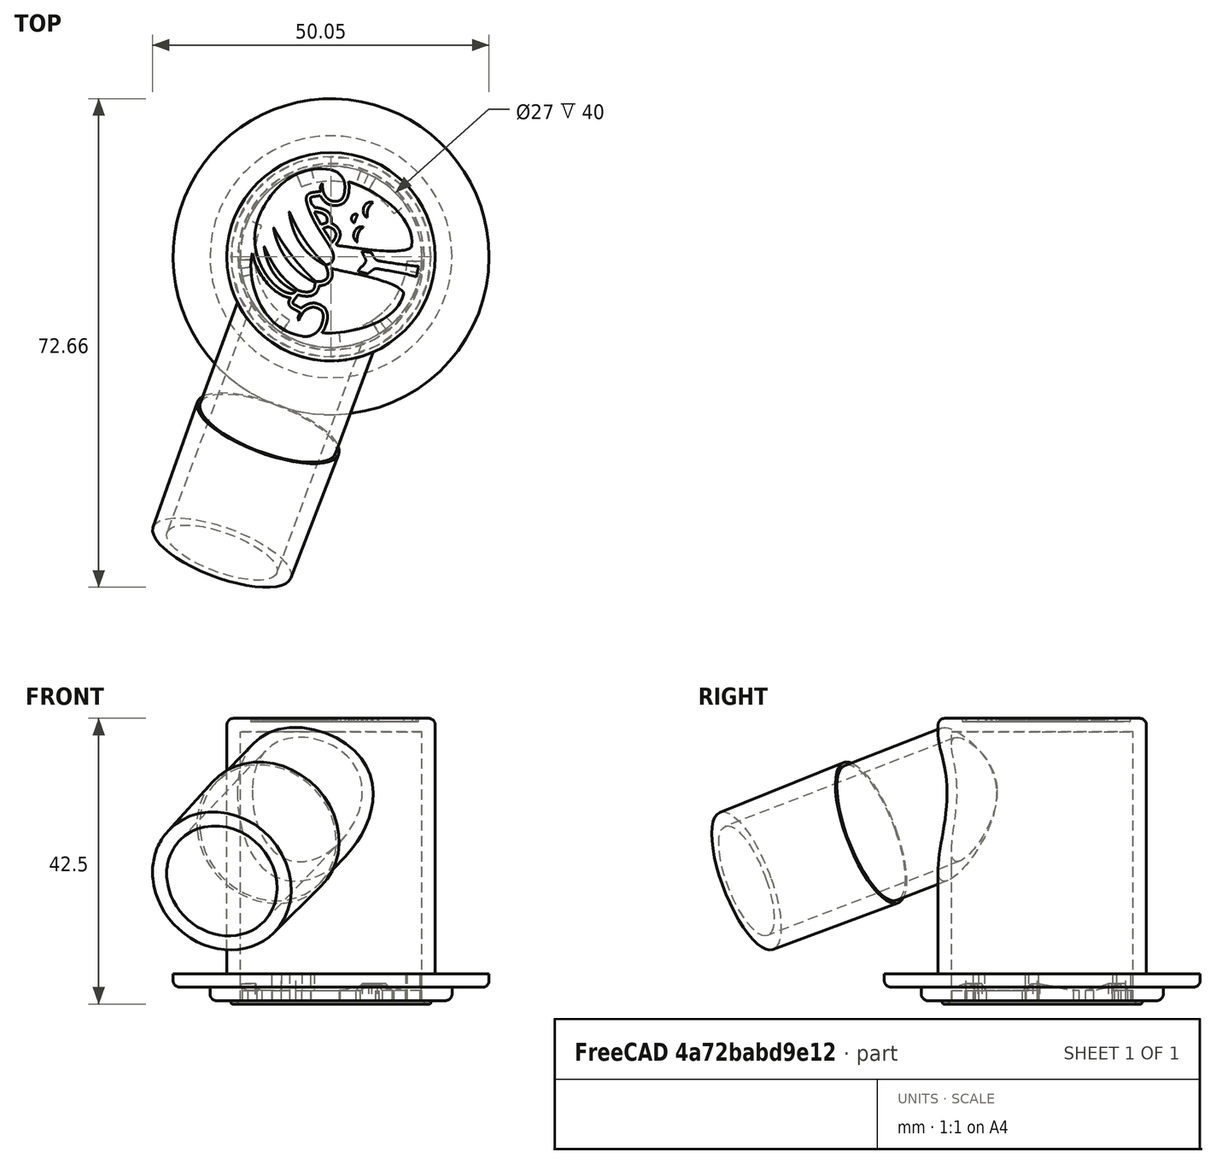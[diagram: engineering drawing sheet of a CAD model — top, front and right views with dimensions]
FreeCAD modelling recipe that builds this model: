
FCSTD DOCUMENT  (FreeCAD 0.18R4 (GitTag))
Label: PAPR-MaskAdapter-V2
License: All rights reserved
LicenseURL: http://en.wikipedia.org/wiki/All_rights_reserved
objects: Sketcher::SketchObject×40, Part::Sweep×16, Part::MultiFuse×13, Part::Feature×10, Part::Extrusion×10, Part::Cylinder×6, Part::Mirroring×5, Part::Fillet×4, Part::Cut×4, Part::FeaturePython×2, PartDesign::Body×1, Mesh::Feature×1, Part::Cone×1
note: 112 computed .brp shape members not serialized (recipe doc carries the construction recipe); baked Part::Feature solids carry a one-line shape summary decoded from their .brp

FEATURE [Sketcher::SketchObject] Sketch  label="RampStart"
  Placement = pos=(0,0,0) rot=(1,0,0;1.5708rad)
  sketch-geometry (4):
    g0: LineSegment StartX=-13.5 StartY=0 StartZ=0 EndX=-13.5 EndY=1.5 EndZ=0
    g1: LineSegment StartX=-13.5 StartY=1.5 StartZ=0 EndX=-11.3 EndY=1.5 EndZ=0
    g2: LineSegment StartX=-11.3 StartY=1.5 StartZ=0 EndX=-11.3 EndY=0 EndZ=0
    g3: LineSegment StartX=-11.3 StartY=0 StartZ=0 EndX=-13.5 EndY=0 EndZ=0
  constraints (12):
    c: Coincident(g0,g1)
    c: Coincident(g1,g2)
    c: Coincident(g2,g3)
    c: Coincident(g3,g0)
    c: Parallel(g0,g2)
    c: Parallel(g1,g3)
    c: Horizontal(g3)
    c: Vertical(g2)
    c: DistanceY(g-1,g2) = 0
    c: DistanceX(g2,g-1) = 11.3
    c: DistanceX(g0,g-1) = 13.5
    c: DistanceY(g0,g0) = 1.5
FEATURE [Sketcher::SketchObject] Sketch001  label="InnerCircumference"
  Placement = pos=(0,0,0) rot=(1,0,0;3.14159rad)
  sketch-geometry (1):
    g0: Circle CenterX=0 CenterY=0 CenterZ=0 NormalX=0 NormalY=0 NormalZ=1 AngleXU=0 Radius=11
  constraints (1):
    c: Radius(g0) = 11
FEATURE [Sketcher::SketchObject] Sketch002  label="RampEnd"
  Placement = pos=(0,0,0) rot=(0.950615,-0.219467,-0.219467;1.62142rad)
  sketch-geometry (4):
    g0: LineSegment StartX=-13.5 StartY=0 StartZ=0 EndX=-13.5 EndY=2.5 EndZ=0
    g1: LineSegment StartX=-13.5 StartY=2.5 StartZ=0 EndX=-11.3 EndY=2.5 EndZ=0
    g2: LineSegment StartX=-11.3 StartY=2.5 StartZ=0 EndX=-11.3 EndY=0 EndZ=0
    g3: LineSegment StartX=-11.3 StartY=0 StartZ=0 EndX=-13.5 EndY=0 EndZ=0
  constraints (12):
    c: Coincident(g0,g1)
    c: Coincident(g1,g2)
    c: Coincident(g2,g3)
    c: Coincident(g3,g0)
    c: Parallel(g0,g2)
    c: Parallel(g1,g3)
    c: Horizontal(g3)
    c: Vertical(g2)
    c: DistanceY(g-1,g2) = 0
    c: DistanceX(g2,g-1) = 11.3
    c: DistanceX(g0,g-1) = 13.5
    c: DistanceY(g0,g0) = 2.5
FEATURE [Sketcher::SketchObject] Sketch003  label="RampFlat"
  Placement = pos=(0,0,0) rot=(0.930118,-0.259693,-0.259693;1.64318rad)
  sketch-geometry (4):
    g0: LineSegment StartX=-13.5 StartY=0 StartZ=0 EndX=-13.5 EndY=2.5 EndZ=0
    g1: LineSegment StartX=-13.5 StartY=2.5 StartZ=0 EndX=-11.3 EndY=2.5 EndZ=0
    g2: LineSegment StartX=-11.3 StartY=2.5 StartZ=0 EndX=-11.3 EndY=0 EndZ=0
    g3: LineSegment StartX=-11.3 StartY=0 StartZ=0 EndX=-13.5 EndY=0 EndZ=0
  constraints (12):
    c: Coincident(g0,g1)
    c: Coincident(g1,g2)
    c: Coincident(g2,g3)
    c: Coincident(g3,g0)
    c: Parallel(g0,g2)
    c: Parallel(g1,g3)
    c: Horizontal(g3)
    c: Vertical(g2)
    c: DistanceY(g-1,g2) = 0
    c: DistanceX(g2,g-1) = 11.3
    c: DistanceX(g0,g-1) = 13.5
    c: DistanceY(g0,g0) = 2.5
FEATURE [Sketcher::SketchObject] Sketch004  label="LockFlat"
  Placement = pos=(0,0,0) rot=(0.906297,-0.298852,-0.298852;1.66903rad)
  sketch-geometry (4):
    g0: LineSegment StartX=-13.5 StartY=0 StartZ=0 EndX=-13.5 EndY=1.5 EndZ=0
    g1: LineSegment StartX=-13.5 StartY=1.5 StartZ=0 EndX=-11.3 EndY=1.5 EndZ=0
    g2: LineSegment StartX=-11.3 StartY=1.5 StartZ=0 EndX=-11.3 EndY=0 EndZ=0
    g3: LineSegment StartX=-11.3 StartY=0 StartZ=0 EndX=-13.5 EndY=0 EndZ=0
  constraints (12):
    c: Coincident(g0,g1)
    c: Coincident(g1,g2)
    c: Coincident(g2,g3)
    c: Coincident(g3,g0)
    c: Parallel(g0,g2)
    c: Parallel(g1,g3)
    c: Horizontal(g3)
    c: Vertical(g2)
    c: DistanceY(g-1,g2) = 0
    c: DistanceX(g2,g-1) = 11.3
    c: DistanceX(g0,g-1) = 13.5
    c: DistanceY(g0,g0) = 1.5
FEATURE [Sketcher::SketchObject] Sketch005  label="LockFlatEnd"
  Placement = pos=(0,0,0) rot=(0.638387,-0.544271,-0.544271;2.00526rad)
  sketch-geometry (4):
    g0: LineSegment StartX=-13.5 StartY=0 StartZ=0 EndX=-13.5 EndY=1.5 EndZ=0
    g1: LineSegment StartX=-13.5 StartY=1.5 StartZ=0 EndX=-11.3 EndY=1.5 EndZ=0
    g2: LineSegment StartX=-11.3 StartY=1.5 StartZ=0 EndX=-11.3 EndY=0 EndZ=0
    g3: LineSegment StartX=-11.3 StartY=0 StartZ=0 EndX=-13.5 EndY=0 EndZ=0
  constraints (12):
    c: Coincident(g0,g1)
    c: Coincident(g1,g2)
    c: Coincident(g2,g3)
    c: Coincident(g3,g0)
    c: Parallel(g0,g2)
    c: Parallel(g1,g3)
    c: Horizontal(g3)
    c: Vertical(g2)
    c: DistanceY(g-1,g2) = 0
    c: DistanceX(g2,g-1) = 11.3
    c: DistanceX(g0,g-1) = 13.5
    c: DistanceY(g0,g0) = 1.5
FEATURE [Sketcher::SketchObject] Sketch006  label="RampPath"
  sketch-geometry (1):
    g0: ArcOfCircle CenterX=0 CenterY=0 CenterZ=0 NormalX=0 NormalY=0 NormalZ=1 AngleXU=0 Radius=11.0109 StartAngle=1.68589 EndAngle=3.14182
FEATURE [Sketcher::SketchObject] Sketch007  label="Path1"
  sketch-geometry (2):
    g0: ArcOfCircle CenterX=0 CenterY=0 CenterZ=0 NormalX=0 NormalY=0 NormalZ=1 AngleXU=0 Radius=11.3 StartAngle=2.68754 EndAngle=3.14132
    g1: GeomPoint X=-10.1564 Y=4.95359 Z=0
  constraints (3):
    c: Radius(g0) = 11.3
    c: Coincident(g-1,g0)
    c: Angle(g0) = 0.453786
FEATURE [PartDesign::Body] Body
  Group = -> [Sketch005,Sketch004,Sketch003,Sketch002,Sketch001,Sketch,Sketch006,Sketch007]
  Origin = -> Origin
FEATURE [Part::Sweep] Sweep
  Frenet = false
  Sections = -> [Sketch,Sketch002]
  Solid = true
  Spine = -> Sketch007 [Edge1]
  Transition = 1
FEATURE [Sketcher::SketchObject] Sketch008  label="Path2"
  sketch-geometry (1):
    g0: ArcOfCircle CenterX=0 CenterY=0 CenterZ=0 NormalX=0 NormalY=0 NormalZ=1 AngleXU=0 Radius=11.3 StartAngle=2.59707 EndAngle=2.68754
  constraints (2):
    c: Radius(g0) = 11.3
    c: Coincident(g0,g-1)
FEATURE [Sketcher::SketchObject] Sketch009  label="Path3"
  sketch-geometry (1):
    g0: ArcOfCircle CenterX=0 CenterY=0 CenterZ=0 NormalX=0 NormalY=0 NormalZ=1 AngleXU=0 Radius=11.3 StartAngle=2.50468 EndAngle=2.59704
  constraints (2):
    c: Radius(g0) = 11.3
    c: Coincident(g0,g-1)
FEATURE [Sketcher::SketchObject] Sketch010  label="Path4"
  sketch-geometry (1):
    g0: ArcOfCircle CenterX=0 CenterY=0 CenterZ=0 NormalX=0 NormalY=0 NormalZ=1 AngleXU=0 Radius=11.3 StartAngle=1.72935 EndAngle=2.50452
  constraints (2):
    c: Radius(g0) = 11.3
    c: Coincident(g0,g-1)
FEATURE [Part::Sweep] Sweep001
  Frenet = false
  Sections = -> [Sketch002,Sketch003]
  Solid = true
  Spine = -> Sketch008 [Edge1]
  Transition = 1
FEATURE [Part::Sweep] Sweep002
  Frenet = false
  Sections = -> [Sketch003,Sketch004]
  Solid = true
  Spine = -> Sketch009 [Edge1]
  Transition = 1
FEATURE [Part::Sweep] Sweep003
  Frenet = false
  Sections = -> [Sketch004,Sketch005]
  Solid = true
  Spine = -> Sketch010 [Edge1]
  Transition = 1
FEATURE [Part::MultiFuse] Fusion  label="Ramp"
  Shapes = -> [Sweep,Sweep001,Sweep002,Sweep003]
FEATURE [Sketcher::SketchObject] Sketch011  label="EndstopEnd"
  Placement = pos=(0,0,0) rot=(0.638387,-0.544271,-0.544271;2.00526rad)
  sketch-geometry (4):
    g0: LineSegment StartX=-13.5 StartY=0 StartZ=0 EndX=-13.5 EndY=4 EndZ=0
    g1: LineSegment StartX=-13.5 StartY=4 StartZ=0 EndX=-11.3 EndY=4 EndZ=0
    g2: LineSegment StartX=-11.3 StartY=4 StartZ=0 EndX=-11.3 EndY=0 EndZ=0
    g3: LineSegment StartX=-11.3 StartY=0 StartZ=0 EndX=-13.5 EndY=0 EndZ=0
  constraints (12):
    c: Coincident(g0,g1)
    c: Coincident(g1,g2)
    c: Coincident(g2,g3)
    c: Coincident(g3,g0)
    c: Parallel(g0,g2)
    c: Parallel(g1,g3)
    c: Horizontal(g3)
    c: Vertical(g2)
    c: DistanceY(g-1,g2) = 0
    c: DistanceX(g2,g-1) = 11.3
    c: DistanceX(g0,g-1) = 13.5
    c: DistanceY(g0,g0) = 4
FEATURE [Sketcher::SketchObject] Sketch012  label="EndstopStart"
  Placement = pos=(0,0,0) rot=(0.688237,-0.512996,-0.512996;1.93602rad)
  sketch-geometry (4):
    g0: LineSegment StartX=-13.5 StartY=0 StartZ=0 EndX=-13.5 EndY=4 EndZ=0
    g1: LineSegment StartX=-13.5 StartY=4 StartZ=0 EndX=-11.3 EndY=4 EndZ=0
    g2: LineSegment StartX=-11.3 StartY=4 StartZ=0 EndX=-11.3 EndY=0 EndZ=0
    g3: LineSegment StartX=-11.3 StartY=0 StartZ=0 EndX=-13.5 EndY=0 EndZ=0
  constraints (12):
    c: Coincident(g0,g1)
    c: Coincident(g1,g2)
    c: Coincident(g2,g3)
    c: Coincident(g3,g0)
    c: Parallel(g0,g2)
    c: Parallel(g1,g3)
    c: Horizontal(g3)
    c: Vertical(g2)
    c: DistanceY(g-1,g2) = 0
    c: DistanceX(g2,g-1) = 11.3
    c: DistanceX(g0,g-1) = 13.5
    c: DistanceY(g0,g0) = 4
FEATURE [Sketcher::SketchObject] Sketch013  label="EndstopPath"
  sketch-geometry (1):
    g0: ArcOfCircle CenterX=0 CenterY=0 CenterZ=0 NormalX=0 NormalY=0 NormalZ=1 AngleXU=0 Radius=11.3 StartAngle=1.72959 EndAngle=1.86043
  constraints (2):
    c: Radius(g0) = 11.3
    c: Coincident(g-1,g0)
FEATURE [Part::Sweep] Sweep004  label="EndStop"
  Frenet = false
  Sections = -> [Sketch012,Sketch011]
  Solid = true
  Spine = -> Sketch013 [Edge1]
  Transition = 1
FEATURE [Part::MultiFuse] Fusion001  label="RampWithEndstop"
  Shapes = -> [Fusion,Sweep004]
FEATURE [Part::Cylinder] Cylinder001  label="pBase-Lower"
  Angle = 360
  AttacherType = Attacher::AttachEngine3D
  Height = 2
  Radius = 18
FEATURE [Part::Cylinder] Cylinder002  label="nBody-Chamber"
  Angle = 360
  AttacherType = Attacher::AttachEngine3D
  Height = 40
  Radius = 13.5
FEATURE [Sketcher::SketchObject] Sketch015  label="GrooveProfile"
  Placement = pos=(0,0,0) rot=(1,0,0;1.5708rad)
  sketch-geometry (4):
    g0: LineSegment StartX=-14.875 StartY=-0.5 StartZ=0 EndX=-13.875 EndY=-0.5 EndZ=0
    g1: LineSegment StartX=-13.875 StartY=-0.5 StartZ=0 EndX=-13.875 EndY=0.5 EndZ=0
    g2: LineSegment StartX=-13.875 StartY=0.5 StartZ=0 EndX=-14.875 EndY=0.5 EndZ=0
    g3: LineSegment StartX=-14.875 StartY=0.5 StartZ=0 EndX=-14.875 EndY=-0.5 EndZ=0
  constraints (12):
    c: Coincident(g0,g1)
    c: Coincident(g1,g2)
    c: Coincident(g2,g3)
    c: Coincident(g3,g0)
    c: Horizontal(g0)
    c: Horizontal(g2)
    c: Vertical(g1)
    c: Vertical(g3)
    c: DistanceX(g0,g0) = 1
    c: Equal(g0,g1)
    c: DistanceY(g1,g-1) = -0.5
    c: DistanceX(g1,g-1) = 13.875
FEATURE [Sketcher::SketchObject] Sketch016  label="GroovePath"
  sketch-geometry (1):
    g0: Circle CenterX=0 CenterY=0 CenterZ=0 NormalX=0 NormalY=0 NormalZ=1 AngleXU=0 Radius=13.875
  constraints (2):
    c: Coincident(g0,g-1)
    c: Radius(g0) = 13.875
FEATURE [Part::Sweep] Sweep005  label="pBase-Groove"
  Frenet = false
  Sections = -> [Sketch015]
  Solid = true
  Spine = -> Sketch016 [Edge1]
  Transition = 1
FEATURE [Part::Mirroring] Part__Mirroring  label="RampWithEndstopLong1"
  Base = (2.14696,3.57628e-07,2)
  Normal = (0,1,-1.19209e-07)
  Placement = pos=(0,0,0) rot=(0,0,-1;0.418879rad)
  Source = -> Fusion001
FEATURE [Sketcher::SketchObject] Sketch017  label="RampStart001"
  Placement = pos=(0,0,0) rot=(1,0,0;1.5708rad)
  sketch-geometry (4):
    g0: LineSegment StartX=-13.5 StartY=0 StartZ=0 EndX=-13.5 EndY=1.5 EndZ=0
    g1: LineSegment StartX=-13.5 StartY=1.5 StartZ=0 EndX=-11.3 EndY=1.5 EndZ=0
    g2: LineSegment StartX=-11.3 StartY=1.5 StartZ=0 EndX=-11.3 EndY=0 EndZ=0
    g3: LineSegment StartX=-11.3 StartY=0 StartZ=0 EndX=-13.5 EndY=0 EndZ=0
  constraints (12):
    c: Coincident(g0,g1)
    c: Coincident(g1,g2)
    c: Coincident(g2,g3)
    c: Coincident(g3,g0)
    c: Parallel(g0,g2)
    c: Parallel(g1,g3)
    c: Horizontal(g3)
    c: Vertical(g2)
    c: DistanceY(g-1,g2) = 0
    c: DistanceX(g2,g-1) = 11.3
    c: DistanceX(g0,g-1) = 13.5
    c: DistanceY(g0,g0) = 1.5
FEATURE [Sketcher::SketchObject] Sketch018  label="RampEnd001"
  Placement = pos=(0,0,0) rot=(0.950615,-0.219467,-0.219467;1.62142rad)
  sketch-geometry (4):
    g0: LineSegment StartX=-13.5 StartY=0 StartZ=0 EndX=-13.5 EndY=2.5 EndZ=0
    g1: LineSegment StartX=-13.5 StartY=2.5 StartZ=0 EndX=-11.3 EndY=2.5 EndZ=0
    g2: LineSegment StartX=-11.3 StartY=2.5 StartZ=0 EndX=-11.3 EndY=0 EndZ=0
    g3: LineSegment StartX=-11.3 StartY=0 StartZ=0 EndX=-13.5 EndY=0 EndZ=0
  constraints (12):
    c: Coincident(g0,g1)
    c: Coincident(g1,g2)
    c: Coincident(g2,g3)
    c: Coincident(g3,g0)
    c: Parallel(g0,g2)
    c: Parallel(g1,g3)
    c: Horizontal(g3)
    c: Vertical(g2)
    c: DistanceY(g-1,g2) = 0
    c: DistanceX(g2,g-1) = 11.3
    c: DistanceX(g0,g-1) = 13.5
    c: DistanceY(g0,g0) = 2.5
FEATURE [Sketcher::SketchObject] Sketch019  label="RampFlat001"
  Placement = pos=(0,0,0) rot=(0.930118,-0.259693,-0.259693;1.64318rad)
  sketch-geometry (4):
    g0: LineSegment StartX=-13.5 StartY=0 StartZ=0 EndX=-13.5 EndY=2.5 EndZ=0
    g1: LineSegment StartX=-13.5 StartY=2.5 StartZ=0 EndX=-11.3 EndY=2.5 EndZ=0
    g2: LineSegment StartX=-11.3 StartY=2.5 StartZ=0 EndX=-11.3 EndY=0 EndZ=0
    g3: LineSegment StartX=-11.3 StartY=0 StartZ=0 EndX=-13.5 EndY=0 EndZ=0
  constraints (12):
    c: Coincident(g0,g1)
    c: Coincident(g1,g2)
    c: Coincident(g2,g3)
    c: Coincident(g3,g0)
    c: Parallel(g0,g2)
    c: Parallel(g1,g3)
    c: Horizontal(g3)
    c: Vertical(g2)
    c: DistanceY(g-1,g2) = 0
    c: DistanceX(g2,g-1) = 11.3
    c: DistanceX(g0,g-1) = 13.5
    c: DistanceY(g0,g0) = 2.5
FEATURE [Sketcher::SketchObject] Sketch020  label="LockFlat001"
  Placement = pos=(0,0,0) rot=(0.906297,-0.298852,-0.298852;1.66903rad)
  sketch-geometry (4):
    g0: LineSegment StartX=-13.5 StartY=0 StartZ=0 EndX=-13.5 EndY=1.5 EndZ=0
    g1: LineSegment StartX=-13.5 StartY=1.5 StartZ=0 EndX=-11.3 EndY=1.5 EndZ=0
    g2: LineSegment StartX=-11.3 StartY=1.5 StartZ=0 EndX=-11.3 EndY=0 EndZ=0
    g3: LineSegment StartX=-11.3 StartY=0 StartZ=0 EndX=-13.5 EndY=0 EndZ=0
  constraints (12):
    c: Coincident(g0,g1)
    c: Coincident(g1,g2)
    c: Coincident(g2,g3)
    c: Coincident(g3,g0)
    c: Parallel(g0,g2)
    c: Parallel(g1,g3)
    c: Horizontal(g3)
    c: Vertical(g2)
    c: DistanceY(g-1,g2) = 0
    c: DistanceX(g2,g-1) = 11.3
    c: DistanceX(g0,g-1) = 13.5
    c: DistanceY(g0,g0) = 1.5
FEATURE [Sketcher::SketchObject] Sketch021  label="LockFlatEnd001"
  Placement = pos=(0,0,0) rot=(0.656406,-0.533447,-0.533447;1.97986rad)
  sketch-geometry (4):
    g0: LineSegment StartX=-13.5 StartY=0 StartZ=0 EndX=-13.5 EndY=1.5 EndZ=0
    g1: LineSegment StartX=-13.5 StartY=1.5 StartZ=0 EndX=-11.3 EndY=1.5 EndZ=0
    g2: LineSegment StartX=-11.3 StartY=1.5 StartZ=0 EndX=-11.3 EndY=0 EndZ=0
    g3: LineSegment StartX=-11.3 StartY=0 StartZ=0 EndX=-13.5 EndY=0 EndZ=0
  constraints (12):
    c: Coincident(g0,g1)
    c: Coincident(g1,g2)
    c: Coincident(g2,g3)
    c: Coincident(g3,g0)
    c: Parallel(g0,g2)
    c: Parallel(g1,g3)
    c: Horizontal(g3)
    c: Vertical(g2)
    c: DistanceY(g-1,g2) = 0
    c: DistanceX(g2,g-1) = 11.3
    c: DistanceX(g0,g-1) = 13.5
    c: DistanceY(g0,g0) = 1.5
FEATURE [Sketcher::SketchObject] Sketch022  label="Path005"
  sketch-geometry (2):
    g0: ArcOfCircle CenterX=0 CenterY=0 CenterZ=0 NormalX=0 NormalY=0 NormalZ=1 AngleXU=0 Radius=11.3 StartAngle=2.68754 EndAngle=3.14132
    g1: GeomPoint X=-10.1564 Y=4.95359 Z=0
  constraints (3):
    c: Radius(g0) = 11.3
    c: Coincident(g-1,g0)
    c: Angle(g0) = 0.453786
FEATURE [Sketcher::SketchObject] Sketch023  label="Path006"
  sketch-geometry (1):
    g0: ArcOfCircle CenterX=0 CenterY=0 CenterZ=0 NormalX=0 NormalY=0 NormalZ=1 AngleXU=0 Radius=11.3 StartAngle=2.59707 EndAngle=2.68754
  constraints (2):
    c: Radius(g0) = 11.3
    c: Coincident(g0,g-1)
FEATURE [Sketcher::SketchObject] Sketch024  label="Path007"
  sketch-geometry (1):
    g0: ArcOfCircle CenterX=0 CenterY=0 CenterZ=0 NormalX=0 NormalY=0 NormalZ=1 AngleXU=0 Radius=11.3 StartAngle=2.50468 EndAngle=2.59704
  constraints (2):
    c: Radius(g0) = 11.3
    c: Coincident(g0,g-1)
FEATURE [Sketcher::SketchObject] Sketch025  label="Path008"
  sketch-geometry (1):
    g0: ArcOfCircle CenterX=0 CenterY=0 CenterZ=0 NormalX=0 NormalY=0 NormalZ=1 AngleXU=0 Radius=11.3 StartAngle=1.77654 EndAngle=2.50452
  constraints (2):
    c: Radius(g0) = 11.3
    c: Coincident(g0,g-1)
FEATURE [Part::Sweep] Sweep006
  Frenet = false
  Sections = -> [Sketch018,Sketch019]
  Solid = true
  Spine = -> Sketch023 [Edge1]
  Transition = 1
FEATURE [Part::Sweep] Sweep007
  Frenet = false
  Sections = -> [Sketch019,Sketch020]
  Solid = true
  Spine = -> Sketch024 [Edge1]
  Transition = 1
FEATURE [Part::Sweep] Sweep008
  Frenet = false
  Sections = -> [Sketch020,Sketch021]
  Solid = true
  Spine = -> Sketch025 [Edge1]
  Transition = 1
FEATURE [Sketcher::SketchObject] Sketch026  label="EndstopEnd001"
  Placement = pos=(0,0,0) rot=(0.656406,-0.533447,-0.533447;1.97986rad)
  sketch-geometry (4):
    g0: LineSegment StartX=-13.5 StartY=0 StartZ=0 EndX=-13.5 EndY=4 EndZ=0
    g1: LineSegment StartX=-13.5 StartY=4 StartZ=0 EndX=-11.3 EndY=4 EndZ=0
    g2: LineSegment StartX=-11.3 StartY=4 StartZ=0 EndX=-11.3 EndY=0 EndZ=0
    g3: LineSegment StartX=-11.3 StartY=0 StartZ=0 EndX=-13.5 EndY=0 EndZ=0
  constraints (12):
    c: Coincident(g0,g1)
    c: Coincident(g1,g2)
    c: Coincident(g2,g3)
    c: Coincident(g3,g0)
    c: Parallel(g0,g2)
    c: Parallel(g1,g3)
    c: Horizontal(g3)
    c: Vertical(g2)
    c: DistanceY(g-1,g2) = 0
    c: DistanceX(g2,g-1) = 11.3
    c: DistanceX(g0,g-1) = 13.5
    c: DistanceY(g0,g0) = 4
FEATURE [Sketcher::SketchObject] Sketch027  label="EndstopStart001"
  Placement = pos=(0,0,0) rot=(0.722291,-0.489028,-0.489028;1.89053rad)
  sketch-geometry (4):
    g0: LineSegment StartX=-13.5 StartY=0 StartZ=0 EndX=-13.5 EndY=4 EndZ=0
    g1: LineSegment StartX=-13.5 StartY=4 StartZ=0 EndX=-11.3 EndY=4 EndZ=0
    g2: LineSegment StartX=-11.3 StartY=4 StartZ=0 EndX=-11.3 EndY=0 EndZ=0
    g3: LineSegment StartX=-11.3 StartY=0 StartZ=0 EndX=-13.5 EndY=0 EndZ=0
  constraints (12):
    c: Coincident(g0,g1)
    c: Coincident(g1,g2)
    c: Coincident(g2,g3)
    c: Coincident(g3,g0)
    c: Parallel(g0,g2)
    c: Parallel(g1,g3)
    c: Horizontal(g3)
    c: Vertical(g2)
    c: DistanceY(g-1,g2) = 0
    c: DistanceX(g2,g-1) = 11.3
    c: DistanceX(g0,g-1) = 13.5
    c: DistanceY(g0,g0) = 4
FEATURE [Sketcher::SketchObject] Sketch028  label="EndstopPath001"
  sketch-geometry (1):
    g0: ArcOfCircle CenterX=0 CenterY=0 CenterZ=0 NormalX=0 NormalY=0 NormalZ=1 AngleXU=0 Radius=11.3 StartAngle=1.77684 EndAngle=1.95126
  constraints (2):
    c: Radius(g0) = 11.3
    c: Coincident(g-1,g0)
FEATURE [Part::Sweep] Sweep009  label="EndStop001"
  Frenet = false
  Sections = -> [Sketch027,Sketch026]
  Solid = true
  Spine = -> Sketch028 [Edge1]
  Transition = 1
FEATURE [Part::Sweep] Sweep010
  Frenet = false
  Sections = -> [Sketch017,Sketch018]
  Solid = true
  Spine = -> Sketch022 [Edge1]
  Transition = 1
FEATURE [Part::MultiFuse] Fusion003  label="Ramp001"
  Shapes = -> [Sweep010,Sweep006,Sweep007,Sweep008]
FEATURE [Part::MultiFuse] Fusion002  label="RampWithEndstopShort"
  Placement = pos=(0,0,0) rot=(0,0,1;0.139626rad)
  Shapes = -> [Fusion003,Sweep009]
FEATURE [Part::Mirroring] Part__Mirroring001  label="RampWithEndstopShort 1"
  Base = (-7.97635,3.57628e-07,2)
  Normal = (0,1,-1.19209e-07)
  Placement = pos=(0,0,0) rot=(0,0,1;3.88336rad)
  Source = -> Fusion002
FEATURE [Sketcher::SketchObject] Sketch029  label="RampStart002"
  Placement = pos=(0,0,0) rot=(1,0,0;1.5708rad)
  sketch-geometry (4):
    g0: LineSegment StartX=-13.5 StartY=0 StartZ=0 EndX=-13.5 EndY=1.5 EndZ=0
    g1: LineSegment StartX=-13.5 StartY=1.5 StartZ=0 EndX=-11.3 EndY=1.5 EndZ=0
    g2: LineSegment StartX=-11.3 StartY=1.5 StartZ=0 EndX=-11.3 EndY=0 EndZ=0
    g3: LineSegment StartX=-11.3 StartY=0 StartZ=0 EndX=-13.5 EndY=0 EndZ=0
  constraints (12):
    c: Coincident(g0,g1)
    c: Coincident(g1,g2)
    c: Coincident(g2,g3)
    c: Coincident(g3,g0)
    c: Parallel(g0,g2)
    c: Parallel(g1,g3)
    c: Horizontal(g3)
    c: Vertical(g2)
    c: DistanceY(g-1,g2) = 0
    c: DistanceX(g2,g-1) = 11.3
    c: DistanceX(g0,g-1) = 13.5
    c: DistanceY(g0,g0) = 1.5
FEATURE [Sketcher::SketchObject] Sketch030  label="RampEnd002"
  Placement = pos=(0,0,0) rot=(0.950615,-0.219467,-0.219467;1.62142rad)
  sketch-geometry (4):
    g0: LineSegment StartX=-13.5 StartY=0 StartZ=0 EndX=-13.5 EndY=2.5 EndZ=0
    g1: LineSegment StartX=-13.5 StartY=2.5 StartZ=0 EndX=-11.3 EndY=2.5 EndZ=0
    g2: LineSegment StartX=-11.3 StartY=2.5 StartZ=0 EndX=-11.3 EndY=0 EndZ=0
    g3: LineSegment StartX=-11.3 StartY=0 StartZ=0 EndX=-13.5 EndY=0 EndZ=0
  constraints (12):
    c: Coincident(g0,g1)
    c: Coincident(g1,g2)
    c: Coincident(g2,g3)
    c: Coincident(g3,g0)
    c: Parallel(g0,g2)
    c: Parallel(g1,g3)
    c: Horizontal(g3)
    c: Vertical(g2)
    c: DistanceY(g-1,g2) = 0
    c: DistanceX(g2,g-1) = 11.3
    c: DistanceX(g0,g-1) = 13.5
    c: DistanceY(g0,g0) = 2.5
FEATURE [Sketcher::SketchObject] Sketch031  label="RampFlat002"
  Placement = pos=(0,0,0) rot=(0.930118,-0.259693,-0.259693;1.64318rad)
  sketch-geometry (4):
    g0: LineSegment StartX=-13.5 StartY=0 StartZ=0 EndX=-13.5 EndY=2.5 EndZ=0
    g1: LineSegment StartX=-13.5 StartY=2.5 StartZ=0 EndX=-11.3 EndY=2.5 EndZ=0
    g2: LineSegment StartX=-11.3 StartY=2.5 StartZ=0 EndX=-11.3 EndY=0 EndZ=0
    g3: LineSegment StartX=-11.3 StartY=0 StartZ=0 EndX=-13.5 EndY=0 EndZ=0
  constraints (12):
    c: Coincident(g0,g1)
    c: Coincident(g1,g2)
    c: Coincident(g2,g3)
    c: Coincident(g3,g0)
    c: Parallel(g0,g2)
    c: Parallel(g1,g3)
    c: Horizontal(g3)
    c: Vertical(g2)
    c: DistanceY(g-1,g2) = 0
    c: DistanceX(g2,g-1) = 11.3
    c: DistanceX(g0,g-1) = 13.5
    c: DistanceY(g0,g0) = 2.5
FEATURE [Sketcher::SketchObject] Sketch032  label="LockFlat002"
  Placement = pos=(0,0,0) rot=(0.906297,-0.298852,-0.298852;1.66903rad)
  sketch-geometry (4):
    g0: LineSegment StartX=-13.5 StartY=0 StartZ=0 EndX=-13.5 EndY=1.5 EndZ=0
    g1: LineSegment StartX=-13.5 StartY=1.5 StartZ=0 EndX=-11.3 EndY=1.5 EndZ=0
    g2: LineSegment StartX=-11.3 StartY=1.5 StartZ=0 EndX=-11.3 EndY=0 EndZ=0
    g3: LineSegment StartX=-11.3 StartY=0 StartZ=0 EndX=-13.5 EndY=0 EndZ=0
  constraints (12):
    c: Coincident(g0,g1)
    c: Coincident(g1,g2)
    c: Coincident(g2,g3)
    c: Coincident(g3,g0)
    c: Parallel(g0,g2)
    c: Parallel(g1,g3)
    c: Horizontal(g3)
    c: Vertical(g2)
    c: DistanceY(g-1,g2) = 0
    c: DistanceX(g2,g-1) = 11.3
    c: DistanceX(g0,g-1) = 13.5
    c: DistanceY(g0,g0) = 1.5
FEATURE [Sketcher::SketchObject] Sketch033  label="LockFlatEnd002"
  Placement = pos=(0,0,0) rot=(0.638387,-0.544271,-0.544271;2.00526rad)
  sketch-geometry (4):
    g0: LineSegment StartX=-13.5 StartY=0 StartZ=0 EndX=-13.5 EndY=1.5 EndZ=0
    g1: LineSegment StartX=-13.5 StartY=1.5 StartZ=0 EndX=-11.3 EndY=1.5 EndZ=0
    g2: LineSegment StartX=-11.3 StartY=1.5 StartZ=0 EndX=-11.3 EndY=0 EndZ=0
    g3: LineSegment StartX=-11.3 StartY=0 StartZ=0 EndX=-13.5 EndY=0 EndZ=0
  constraints (12):
    c: Coincident(g0,g1)
    c: Coincident(g1,g2)
    c: Coincident(g2,g3)
    c: Coincident(g3,g0)
    c: Parallel(g0,g2)
    c: Parallel(g1,g3)
    c: Horizontal(g3)
    c: Vertical(g2)
    c: DistanceY(g-1,g2) = 0
    c: DistanceX(g2,g-1) = 11.3
    c: DistanceX(g0,g-1) = 13.5
    c: DistanceY(g0,g0) = 1.5
FEATURE [Sketcher::SketchObject] Sketch034  label="Path009"
  sketch-geometry (2):
    g0: ArcOfCircle CenterX=0 CenterY=0 CenterZ=0 NormalX=0 NormalY=0 NormalZ=1 AngleXU=0 Radius=11.3 StartAngle=2.68754 EndAngle=3.14132
    g1: GeomPoint X=-10.1564 Y=4.95359 Z=0
  constraints (3):
    c: Radius(g0) = 11.3
    c: Coincident(g-1,g0)
    c: Angle(g0) = 0.453786
FEATURE [Part::Sweep] Sweep011
  Frenet = false
  Sections = -> [Sketch029,Sketch030]
  Solid = true
  Spine = -> Sketch034 [Edge1]
  Transition = 1
FEATURE [Sketcher::SketchObject] Sketch035  label="Path010"
  sketch-geometry (1):
    g0: ArcOfCircle CenterX=0 CenterY=0 CenterZ=0 NormalX=0 NormalY=0 NormalZ=1 AngleXU=0 Radius=11.3 StartAngle=2.59707 EndAngle=2.68754
  constraints (2):
    c: Radius(g0) = 11.3
    c: Coincident(g0,g-1)
FEATURE [Sketcher::SketchObject] Sketch036  label="Path011"
  sketch-geometry (1):
    g0: ArcOfCircle CenterX=0 CenterY=0 CenterZ=0 NormalX=0 NormalY=0 NormalZ=1 AngleXU=0 Radius=11.3 StartAngle=2.50468 EndAngle=2.59704
  constraints (2):
    c: Radius(g0) = 11.3
    c: Coincident(g0,g-1)
FEATURE [Sketcher::SketchObject] Sketch037  label="Path012"
  sketch-geometry (1):
    g0: ArcOfCircle CenterX=0 CenterY=0 CenterZ=0 NormalX=0 NormalY=0 NormalZ=1 AngleXU=0 Radius=11.3 StartAngle=1.72961 EndAngle=2.50452
  constraints (2):
    c: Radius(g0) = 11.3
    c: Coincident(g0,g-1)
FEATURE [Part::Sweep] Sweep012
  Frenet = false
  Sections = -> [Sketch030,Sketch031]
  Solid = true
  Spine = -> Sketch035 [Edge1]
  Transition = 1
FEATURE [Part::Sweep] Sweep013
  Frenet = false
  Sections = -> [Sketch031,Sketch032]
  Solid = true
  Spine = -> Sketch036 [Edge1]
  Transition = 1
FEATURE [Part::Sweep] Sweep014
  Frenet = false
  Sections = -> [Sketch032,Sketch033]
  Solid = true
  Spine = -> Sketch037 [Edge1]
  Transition = 1
FEATURE [Part::MultiFuse] Fusion004  label="Ramp002"
  Shapes = -> [Sweep011,Sweep012,Sweep013,Sweep014]
FEATURE [Sketcher::SketchObject] Sketch038  label="EndstopEnd002"
  Placement = pos=(0,0,0) rot=(0.638387,-0.544271,-0.544271;2.00526rad)
  sketch-geometry (4):
    g0: LineSegment StartX=-13.5 StartY=0 StartZ=0 EndX=-13.5 EndY=4 EndZ=0
    g1: LineSegment StartX=-13.5 StartY=4 StartZ=0 EndX=-11.3 EndY=4 EndZ=0
    g2: LineSegment StartX=-11.3 StartY=4 StartZ=0 EndX=-11.3 EndY=0 EndZ=0
    g3: LineSegment StartX=-11.3 StartY=0 StartZ=0 EndX=-13.5 EndY=0 EndZ=0
  constraints (12):
    c: Coincident(g0,g1)
    c: Coincident(g1,g2)
    c: Coincident(g2,g3)
    c: Coincident(g3,g0)
    c: Parallel(g0,g2)
    c: Parallel(g1,g3)
    c: Horizontal(g3)
    c: Vertical(g2)
    c: DistanceY(g-1,g2) = 0
    c: DistanceX(g2,g-1) = 11.3
    c: DistanceX(g0,g-1) = 13.5
    c: DistanceY(g0,g0) = 4
FEATURE [Sketcher::SketchObject] Sketch039  label="EndstopStart002"
  Placement = pos=(0,0,0) rot=(0.688237,-0.512996,-0.512996;1.93602rad)
  sketch-geometry (4):
    g0: LineSegment StartX=-13.5 StartY=0 StartZ=0 EndX=-13.5 EndY=4 EndZ=0
    g1: LineSegment StartX=-13.5 StartY=4 StartZ=0 EndX=-11.3 EndY=4 EndZ=0
    g2: LineSegment StartX=-11.3 StartY=4 StartZ=0 EndX=-11.3 EndY=0 EndZ=0
    g3: LineSegment StartX=-11.3 StartY=0 StartZ=0 EndX=-13.5 EndY=0 EndZ=0
  constraints (12):
    c: Coincident(g0,g1)
    c: Coincident(g1,g2)
    c: Coincident(g2,g3)
    c: Coincident(g3,g0)
    c: Parallel(g0,g2)
    c: Parallel(g1,g3)
    c: Horizontal(g3)
    c: Vertical(g2)
    c: DistanceY(g-1,g2) = 0
    c: DistanceX(g2,g-1) = 11.3
    c: DistanceX(g0,g-1) = 13.5
    c: DistanceY(g0,g0) = 4
FEATURE [Sketcher::SketchObject] Sketch040  label="EndstopPath002"
  sketch-geometry (1):
    g0: ArcOfCircle CenterX=0 CenterY=0 CenterZ=0 NormalX=0 NormalY=0 NormalZ=1 AngleXU=0 Radius=11.3 StartAngle=1.72959 EndAngle=1.86043
  constraints (2):
    c: Radius(g0) = 11.3
    c: Coincident(g-1,g0)
FEATURE [Part::Sweep] Sweep015  label="EndStop002"
  Frenet = false
  Sections = -> [Sketch039,Sketch038]
  Solid = true
  Spine = -> Sketch040 [Edge1]
  Transition = 1
FEATURE [Part::MultiFuse] Fusion005  label="RampWithEndstop001"
  Shapes = -> [Fusion004,Sweep015]
FEATURE [Part::Mirroring] Part__Mirroring002  label="RampWithEndstopLong2"
  Base = (2.14696,3.57628e-07,2)
  Normal = (0,1,-1.19209e-07)
  Placement = pos=(0,0,0) rot=(0,0,1;1.67552rad)
  Source = -> Fusion005
FEATURE [Part::MultiFuse] Fusion006  label="Ramps"
  Shapes = -> [Part__Mirroring002,Part__Mirroring001,Part__Mirroring]
FEATURE [Mesh::Feature] BayonetMtestV2
  Placement = pos=(0,0,-1.8) rot=(0,0,1;1.02102rad)
FEATURE [Part::Cylinder] Cylinder003  label="pBody-Chamber"
  Angle = 360
  AttacherType = Attacher::AttachEngine3D
  Height = 42
  Radius = 15.5
FEATURE [Part::Cylinder] Cylinder004  label="pBase-Upper"
  Angle = 360
  AttacherType = Attacher::AttachEngine3D
  Height = 2
  Placement = pos=(0,0,2) rot=(0,0,1;0rad)
  Radius = 23.5
FEATURE [Part::Fillet] Fillet  label="pBody-ChamberRounded"
  Base = -> Cylinder003
  Edges = 1 edges r=1: [Edge1]
FEATURE [Part::Fillet] Fillet001  label="pBase-UpperRounded"
  Base = -> Cylinder004
  Edges = 1 edges r=1: [Edge3]
FEATURE [Part::Fillet] Fillet002  label="pBase-LowerRounded"
  Base = -> Cylinder001
  Edges = 1 edges r=1: [Edge3]
FEATURE [Part::Fillet] Fillet003  label="pBase-GrooveRounded"
  Base = -> Sweep005
  Edges = 2 edges r=0.25: [Edge1,Edge3]
FEATURE [Part::MultiFuse] Fusion007  label="pBody"
  Shapes = -> [Fillet001,Fillet002,Fillet003,Fillet]
FEATURE [Part::Cut] Cut  label="MaskAdapterBody"
  Base = -> Fusion007
  Tool = -> Cylinder002
FEATURE [Part::Cylinder] Cylinder019  label="HousingOutlet"
  Angle = 360
  AttacherType = Attacher::AttachEngine3D
  Height = 40
  Radius = 10.75
FEATURE [Part::Cylinder] Cylinder005  label="OutletExtension"
  Angle = 360
  AttacherType = Attacher::AttachEngine3D
  Height = 40
  Radius = 8.7
FEATURE [Part::Cone] Cone001  label="22mmTaper"
  Angle = 360
  AttacherType = Attacher::AttachEngine3D
  Height = 21
  Placement = pos=(0,0,19) rot=(0,0,1;0rad)
  Radius1 = 11.19
  Radius2 = 10.92
FEATURE [Part::MultiFuse] Fusion020  label="Outside"
  Shapes = -> [Cone001,Cylinder019]
FEATURE [Part::Cut] Cut001  label="22mmHoseTaper"
  Base = -> Fusion020
  Placement = pos=(-3.17239,-8.74374,31.4472) rot=(0.132431,0.813059,-0.566919;3.36248rad)
  Tool = -> Cylinder005
FEATURE [Part::Feature] Face019
  shape: bbox 23.98 x 15.22 x 2e-07 mm, 1 faces, 0 solids (baked)
FEATURE [Part::Feature] Face021
  shape: bbox 2.22 x 2.625 x 2e-07 mm, 1 faces, 0 solids (baked)
FEATURE [Part::Feature] Face022
  shape: bbox 2.744 x 2.564 x 2e-07 mm, 1 faces, 0 solids (baked)
FEATURE [Part::Feature] Face027
  shape: bbox 3.153 x 1.741 x 2e-07 mm, 1 faces, 0 solids (baked)
FEATURE [Part::Feature] Face028
  shape: bbox 12.09 x 20.21 x 2e-07 mm, 1 faces, 0 solids (baked)
FEATURE [Part::Feature] Face020
  shape: bbox 13.56 x 15.09 x 2e-07 mm, 1 faces, 0 solids (baked)
FEATURE [Part::Extrusion] Extrude027  label="n-m-LeftEye"
  Base = -> Face027
  Dir = (0,0,-1)
  DirMode = 2
  FaceMakerClass = Part::FaceMakerBullseye
  LengthFwd = 1
  LengthRev = 0
  Solid = false
  Symmetric = false
FEATURE [Part::Extrusion] Extrude019  label="p-m-LeftHand"
  Base = -> Face019
  Dir = (0,0,-1)
  DirMode = 2
  FaceMakerClass = Part::FaceMakerBullseye
  LengthFwd = 1
  LengthRev = 0
  Solid = false
  Symmetric = false
FEATURE [Part::Extrusion] Extrude021  label="p-m-LeftFinger"
  Base = -> Face021
  Dir = (0,0,-1)
  DirMode = 2
  FaceMakerClass = Part::FaceMakerBullseye
  LengthFwd = 1
  LengthRev = 0
  Solid = false
  Symmetric = false
FEATURE [Part::Extrusion] Extrude022  label="p-m-RightFinger"
  Base = -> Face022
  Dir = (0,0,-1)
  DirMode = 2
  FaceMakerClass = Part::FaceMakerBullseye
  LengthFwd = 1
  LengthRev = 0
  Solid = false
  Symmetric = false
FEATURE [Part::Extrusion] Extrude020  label="p-m-RightHand"
  Base = -> Face020
  Dir = (0,0,-1)
  DirMode = 2
  FaceMakerClass = Part::FaceMakerBullseye
  LengthFwd = 1
  LengthRev = 0
  Solid = false
  Symmetric = false
FEATURE [Part::Extrusion] Extrude028  label="p-LeftLung"
  Base = -> Face028
  Dir = (0,0,1)
  DirMode = 2
  FaceMakerClass = Part::FaceMakerBullseye
  LengthFwd = 1
  LengthRev = 0
  Solid = false
  Symmetric = false
FEATURE [Part::Feature] Face025
  shape: bbox 3.134 x 1.688 x 2e-07 mm, 1 faces, 0 solids (baked)
FEATURE [Part::Extrusion] Extrude025  label="n-m-RightEye"
  Base = -> Face025
  Dir = (0,0,-1)
  DirMode = 2
  FaceMakerClass = Part::FaceMakerBullseye
  LengthFwd = 1
  LengthRev = 0
  Solid = false
  Symmetric = false
FEATURE [Part::Feature] Face026
  shape: bbox 1.76 x 1.081 x 2e-07 mm, 1 faces, 0 solids (baked)
FEATURE [Part::Extrusion] Extrude026  label="n-m-Mouth"
  Base = -> Face026
  Dir = (0,0,-1)
  DirMode = 2
  FaceMakerClass = Part::FaceMakerBullseye
  LengthFwd = 1
  LengthRev = 0
  Solid = false
  Symmetric = false
FEATURE [Part::MultiFuse] Fusion060  label="n-m-Face"
  Shapes = -> [Extrude027,Extrude026,Extrude025]
FEATURE [Part::Mirroring] Part__Mirroring003  label="nLogo (Mirror #1)"
  Base = (0,0,0)
  Normal = (0,0,1)
  Source = -> Fusion060
FEATURE [Part::Feature] Face023
  shape: bbox 4.011 x 10.85 x 2e-07 mm, 1 faces, 0 solids (baked)
FEATURE [Part::Extrusion] Extrude023  label="p-Trachea"
  Base = -> Face023
  Dir = (0,0,1)
  DirMode = 2
  FaceMakerClass = Part::FaceMakerBullseye
  LengthFwd = 1
  LengthRev = 0
  Solid = false
  Symmetric = false
FEATURE [Part::Feature] Face024
  shape: bbox 12.13 x 20.08 x 2e-07 mm, 1 faces, 0 solids (baked)
FEATURE [Part::Extrusion] Extrude024  label="p-m-RightLung"
  Base = -> Face024
  Dir = (0,0,-1)
  DirMode = 2
  FaceMakerClass = Part::FaceMakerBullseye
  LengthFwd = 1
  LengthRev = 0
  Solid = false
  Symmetric = false
FEATURE [Part::MultiFuse] Fusion059  label="p-m-Lungs"
  Shapes = -> [Extrude024,Extrude022,Extrude021,Extrude020,Extrude019]
FEATURE [Part::Mirroring] Part__Mirroring004  label="p-m-Lungs (Mirror #2)"
  Base = (0,0,0)
  Normal = (0,0,1)
  Source = -> Fusion059
FEATURE [Part::MultiFuse] Fusion058  label="pLogo"
  Shapes = -> [Part__Mirroring004,Extrude028,Extrude023]
FEATURE [Part::Cut] Cut019  label="Logo"
  Base = -> Fusion058
  Placement = pos=(-21,16.5,44) rot=(0,0,1;0rad)
  Tool = -> Part__Mirroring003
FEATURE [Part::FeaturePython] Clone  label="LogoCloneScaled"  # Draft clone (typed FeaturePython)
  AttacherType = Attacher::AttachEngine3D
  Fuse = false
  Objects = -> [Cut019]
  Placement = pos=(15.1672,10.911,41.5) rot=(0,0,-1;1.74533rad)
  Scale = (0.8,0.8,0.5)
FEATURE [Part::FeaturePython] Connect  label="AdapterHat"  # WARN: FeaturePython — macro-defined, semantics opaque (R4)
  Objects = -> [Cut001,Cut]
  Tolerance = 0
FEATURE [Part::Cut] Cut020  label="AdapterHatEmbossed"
  Base = -> Connect
  Tool = -> Clone
FEATURE [Part::MultiFuse] Fusion061  label="TopLevelPart-MaskAdapter"
  Shapes = -> [Fusion006,Cut020]
